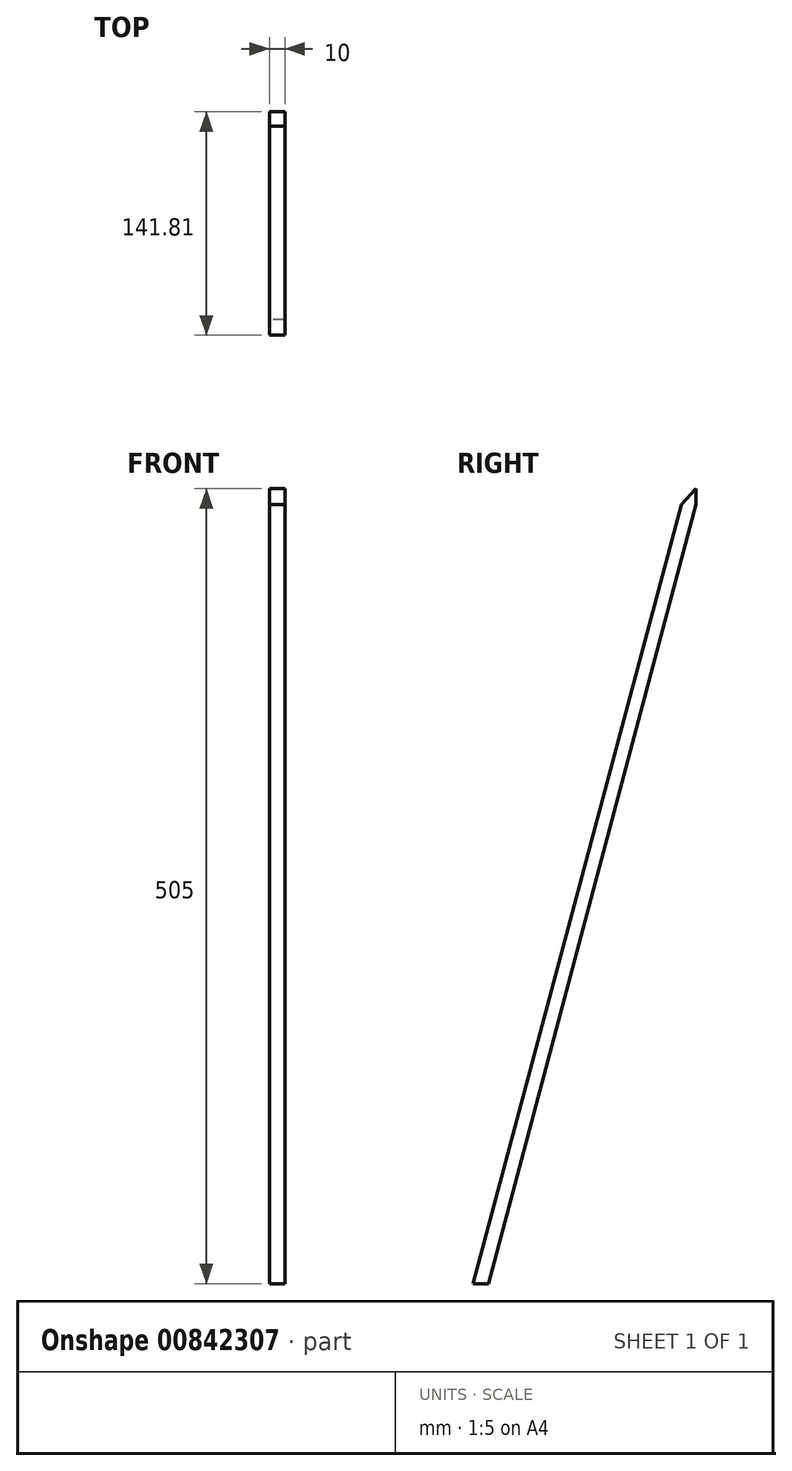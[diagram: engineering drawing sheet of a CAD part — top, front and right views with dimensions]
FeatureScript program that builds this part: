
annotation { "Feature Type Name" : "Feature", "Feature Type Description" : "" }
export const myFeature = defineFeature(function(context is Context, id is Id, definition is map)
    precondition{}
    {
        {
            var Q0;
            Q0=qCreatedBy(makeId("Top.planeOp"),FACE);
            var sketch = newSketch(context, id + "F0", { "sketchPlane" : qUnion([Q0])});
            skLineSegment(sketch, "E0", {"start": v(-42.83, 83.47) * mm, "end": v(-42.83, -58.34) * mm});
            skLineSegment(sketch, "E1", {"start": v(-42.83, 83.47) * mm, "end": v(-32.83, 83.47) * mm});
            skLineSegment(sketch, "E2", {"start": v(-32.83, 83.47) * mm, "end": v(-32.83, -58.34) * mm});
            skLineSegment(sketch, "E3", {"start": v(-42.83, -58.34) * mm, "end": v(-32.83, -58.34) * mm});
            skSolve(sketch);
        }
        {
            var Q0;
            Q0=makeQuery(id+"F0.imprint","IMPRINT",FACE,{"disambiguationData":[TD([[makeQuery(id+"F0.imprint","IMPRINT",EDGE,{"derivedFrom":sQuery(id+"F0.wireOp",EDGE,"E0")}),1.0]])]});
            extrude(context, id + "F1", {"entities" : qUnion([Q0]), "depth" : 495 * mm, "offsetDistance" : 25 * mm});
        }
        {
            var Q0;
            Q0=makeQuery(id+"F1.opExtrude","SWEPT_FACE",FACE,{"disambiguationData":[OSD([sQuery(id+"F0.wireOp",EDGE,"E0")])]});
            var sketch = newSketch(context, id + "F2", { "sketchPlane" : qUnion([Q0])});
            skLineSegment(sketch, "E4", {"start": v(58.34, 0) * mm, "end": v(-74.3, 495) * mm});
            skLineSegment(sketch, "E5", {"start": v(58.34, 0) * mm, "end": v(48.34, 0) * mm});
            skLineSegment(sketch, "E6", {"start": v(48.34, 0) * mm, "end": v(-83.47, 495) * mm});
            skSolve(sketch);
        }
        {
            var Q0;
            {var subQ0=sQuery(id+"F2.wireOp",EDGE,"E6");Q0=makeQuery(id+"F2.imprint","IMPRINT",FACE,{"disambiguationData":[TD([[makeQuery(id+"F2.imprint","IMPRINT",EDGE,{"derivedFrom":subQ0}),1.0]])]});}
            var Q1;
            {var subQ0=sQuery(id+"F2.wireOp",EDGE,"E4");Q1=makeQuery(id+"F2.imprint","IMPRINT",FACE,{"disambiguationData":[TD([[makeQuery(id+"F2.imprint","IMPRINT",EDGE,{"derivedFrom":subQ0}),-1.0]])]});}
            extrude(context, id + "F3", {"entities" : qUnion([Q0, Q1]), "operationType" : NewBodyOperationType.REMOVE, "oppositeDirection" : true, "depth" : 10 * mm, "offsetDistance" : 25 * mm});
        }
        {
            var Q0;
            Q0=makeQuery(id+"F1.opExtrude","SWEPT_FACE",FACE,{"disambiguationData":[OSD([sQuery(id+"F0.wireOp",EDGE,"E0")])]});
            var sketch = newSketch(context, id + "F4", { "sketchPlane" : qUnion([Q0])});
            skLineSegment(sketch, "E7", {"start": v(-83.47, 495) * mm, "end": v(-83.47, 505) * mm});
            skLineSegment(sketch, "E8", {"start": v(-74.3, 495) * mm, "end": v(-83.47, 505) * mm});
            skSolve(sketch);
        }
        {
            var Q0;
            Q0=makeQuery(id+"F4.imprint","IMPRINT",FACE,{"disambiguationData":[TD([[makeQuery(id+"F4.imprint","IMPRINT",EDGE,{"derivedFrom":sQuery(id+"F4.wireOp",EDGE,"E7")}),-1.0]])]});
            extrude(context, id + "F5", {"entities" : qUnion([Q0]), "operationType" : NewBodyOperationType.ADD, "depth" : -10 * mm, "offsetDistance" : 25 * mm});
        }
    });
